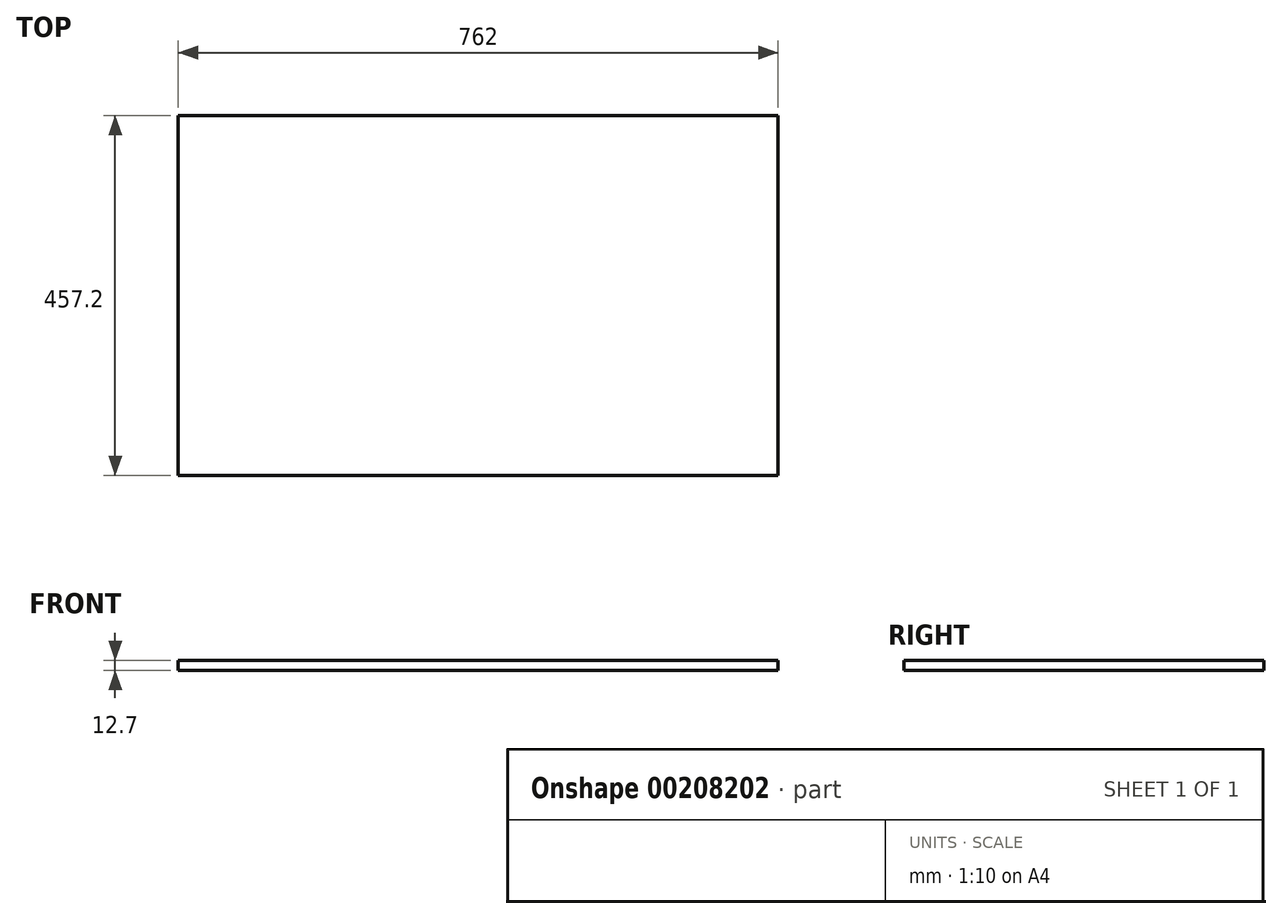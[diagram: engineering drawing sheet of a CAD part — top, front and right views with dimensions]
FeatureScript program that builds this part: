
annotation { "Feature Type Name" : "Feature", "Feature Type Description" : "" }
export const myFeature = defineFeature(function(context is Context, id is Id, definition is map)
    precondition{}
    {
        {
            var Q0;
            Q0=qCreatedBy(makeId("Top.planeOp"),FACE);
            var sketch = newSketch(context, id + "F0", { "sketchPlane" : qUnion([Q0])});
            skLineSegment(sketch, "E0.bottom", {"start": v(-381, 228.6) * mm, "end": v(381, 228.6) * mm});
            skLineSegment(sketch, "E0.top", {"start": v(-381, -228.6) * mm, "end": v(381, -228.6) * mm});
            skLineSegment(sketch, "E0.left", {"start": v(-381, 228.6) * mm, "end": v(-381, -228.6) * mm});
            skLineSegment(sketch, "E0.right", {"start": v(381, 228.6) * mm, "end": v(381, -228.6) * mm});
            skPoint(sketch, "E0.middle", {"position": v(0, 0) * mm});
            skSolve(sketch);
        }
        {
            var Q0;
            Q0 = qSketchRegion(id + "F0", true);
            extrude(context, id + "F1", {"entities" : qUnion([Q0]), "depth" : 12.7 * mm});
        }
    });
